# Revit family: QF_HOSHIZAKI_B-140SA
name_source: partatom
category: Specialty Equipment
revit_build: Autodesk Revit 2016 (Build: 20150220_1215(x64)
units: mm (PartAtom-declared; Revit-internal decimal feet)

## family parameters
Always vertical = Yes
Cut with Voids When Loaded = No
OmniClass Number = 23.40.40.14
OmniClass Title = Food Service Equipment
Part Type = Normal
Room Calculation Point = No
Round Connector Dimension = Use Diameter
Shared = No
Work Plane-Based = No

## types (1)
- B-140SA
    Accessory = No
    Assembly Code = E1090320
    Cost = 0 $
    Depth Actual = 820 mm  [stored 2.69029 ft]
    Description = B SERIES ICE STORAGE BIN, 140 KG CAPACITY
    Height Actual = 1106 mm  [stored 3.62861 ft]
    Indirect Waste Size = 19 mm
    Length Actual = 558 mm
    Manufacturer = HOSHIZAKI
    Model = B-140SA
    URL = www.hoshizaki-europe.com
    Weight = 37.00 kg

note: [stored X ft] marks values corroborated as IEEE doubles in the binary element streams (Revit-internal decimal feet)

## geometry (parser evidence)
native form markers: Sweep x5
no freeform markers — native parametric forms only
